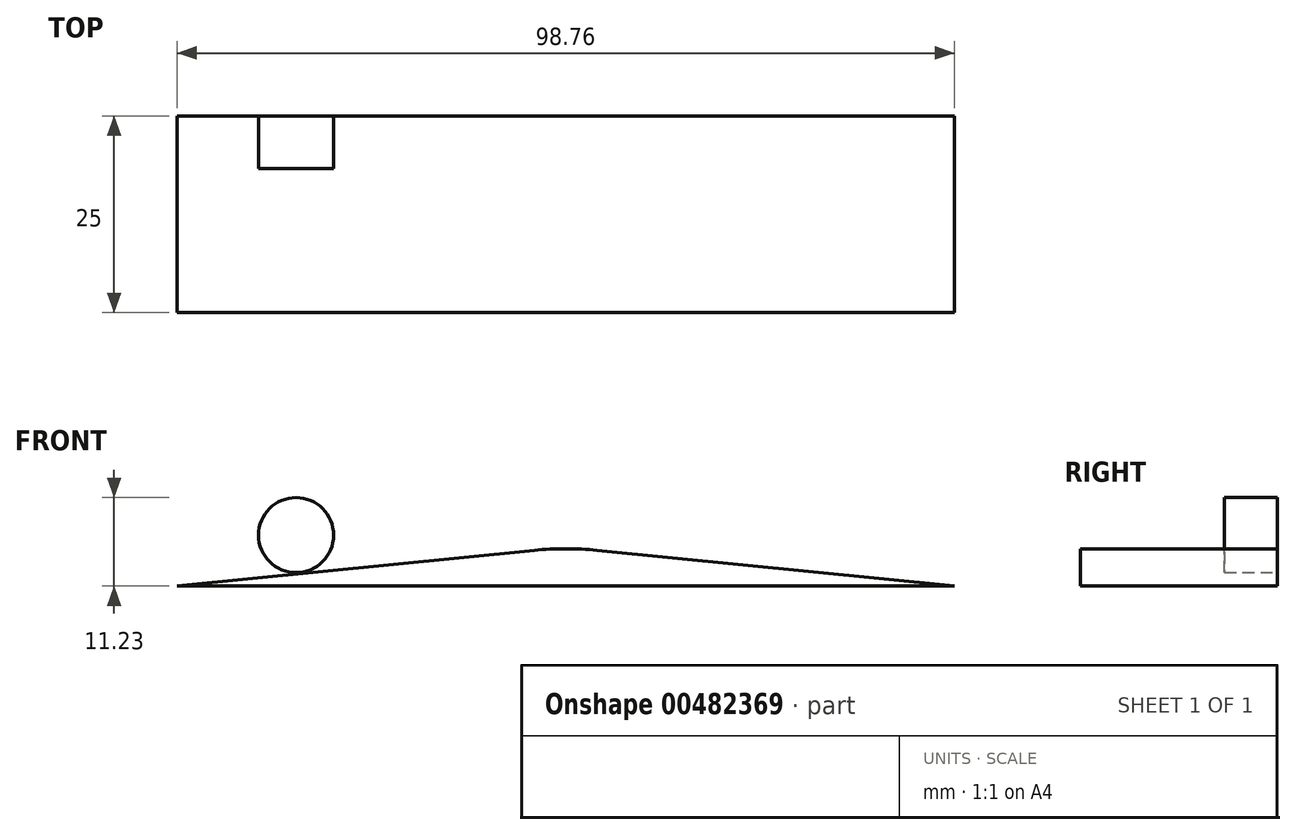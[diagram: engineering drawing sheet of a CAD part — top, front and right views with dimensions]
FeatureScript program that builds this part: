
annotation { "Feature Type Name" : "Feature", "Feature Type Description" : "" }
export const myFeature = defineFeature(function(context is Context, id is Id, definition is map)
    precondition{}
    {
        {
            var Q0;
            Q0=qCreatedBy(makeId("Front.planeOp"),FACE);
            var sketch = newSketch(context, id + "F0", { "sketchPlane" : qUnion([Q0])});
            skLineSegment(sketch, "E0", {"start": v(-49.38, 22.24) * mm, "end": v(0.62, 22.24) * mm});
            skLineSegment(sketch, "E1", {"start": v(0.62, 22.24) * mm, "end": v(0.62, 27.24) * mm});
            skLineSegment(sketch, "E2", {"start": v(0.62, 27.24) * mm, "end": v(-49.38, 22.24) * mm});
            skLineSegment(sketch, "E3.MirrorCS", {"start": v(-0.62, 22.24) * mm, "end": v(-0.62, 27.24) * mm});
            skLineSegment(sketch, "E4.MirrorCS", {"start": v(-0.62, 27.24) * mm, "end": v(49.38, 22.24) * mm});
            skLineSegment(sketch, "E5.MirrorCS", {"start": v(49.38, 22.24) * mm, "end": v(-0.62, 22.24) * mm});
            skSolve(sketch);
        }
        {
            var Q0;
            {var subQ1=sQuery(id+"F0.wireOp",EDGE,"E1");var subQ7=sQuery(id+"F0.wireOp",EDGE,"E5.MirrorCS");var subQ9=makeQuery(id+"F0.imprint","INTERSECT",VERTEX,{"derivedFrom":[subQ1,subQ7]});Q0=makeQuery(id+"F0.imprint","IMPRINT",FACE,{"disambiguationData":[TD([[makeQuery(id+"F0.imprint","IMPRINT",EDGE,{"disambiguationData":[TD([[subQ9,-1.0]])],"derivedFrom":subQ1}),1.0]])]});}
            var Q1;
            {var subQ0=sQuery(id+"F0.wireOp",EDGE,"E5.MirrorCS");var subQ1=sQuery(id+"F0.wireOp",EDGE,"E1");var subQ2=makeQuery(id+"F0.imprint","INTERSECT",VERTEX,{"derivedFrom":[subQ1,subQ0]});Q1=makeQuery(id+"F0.imprint","IMPRINT",FACE,{"disambiguationData":[TD([[makeQuery(id+"F0.imprint","IMPRINT",EDGE,{"disambiguationData":[TD([[subQ2,-1.0]])],"derivedFrom":subQ1}),-1.0]])]});}
            var Q2;
            {var subQ0=sQuery(id+"F0.wireOp",EDGE,"E0");Q2=makeQuery(id+"F0.imprint","IMPRINT",FACE,{"disambiguationData":[TD([[makeQuery(id+"F0.imprint","IMPRINT",EDGE,{"derivedFrom":subQ0}),1.0]])]});}
            extrude(context, id + "F1", {"entities" : qUnion([Q0, Q1, Q2]), "depth" : 25 * mm});
        }
        {
            var Q0;
            Q0=makeQuery(id+"F1.opExtrude","SWEPT_EDGE",EDGE,{"disambiguationData":[OSD([sQuery(id+"F0.wireOp",EDGE,"E2"),sQuery(id+"F0.wireOp",EDGE,"E4.MirrorCS")])]});
            fillet(context, id + "F2", {"entities" : qUnion([Q0]), "radius" : 40.1 * mm, "tangentPropagation" : true, "allowEdgeOverflow" : false});
        }
        {
            var Q0;
            Q0=qCreatedBy(makeId("Front.planeOp"),FACE);
            var sketch = newSketch(context, id + "F3", { "sketchPlane" : qUnion([Q0])});
            skCircle(sketch, "E6", {"center": v(-34.25, 28.7) * mm, "radius": 4.77 * mm});
            skSolve(sketch);
        }
        {
            var Q0;
            Q0=makeQuery(id+"F3.imprint","IMPRINT",FACE,{"disambiguationData":[TD([[makeQuery(id+"F3.imprint","IMPRINT",EDGE,{"derivedFrom":sQuery(id+"F3.wireOp",EDGE,"E6")}),1.0]])]});
            extrude(context, id + "F4", {"entities" : qUnion([Q0]), "depth" : 6.7 * mm});
        }
    });
